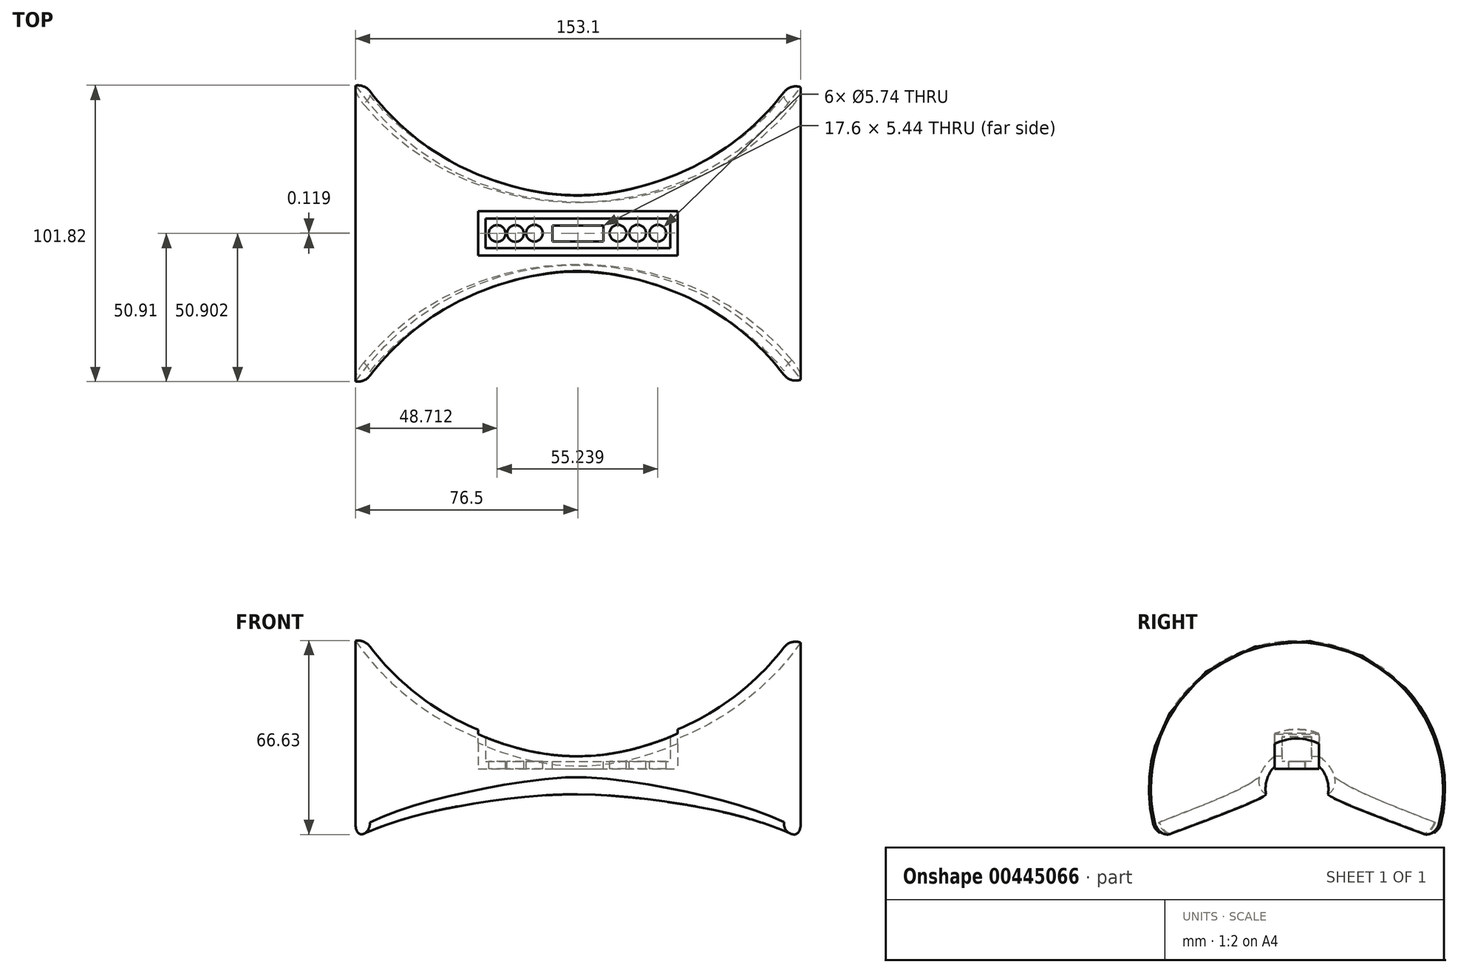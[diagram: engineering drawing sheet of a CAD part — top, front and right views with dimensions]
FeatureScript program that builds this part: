
annotation { "Feature Type Name" : "Feature", "Feature Type Description" : "" }
export const myFeature = defineFeature(function(context is Context, id is Id, definition is map)
    precondition{}
    {
        {
            var Q0;
            Q0=qCreatedBy(makeId("Top.planeOp"),FACE);
            var sketch = newSketch(context, id + "F0", { "sketchPlane" : qUnion([Q0])});
            skArc(sketch, "E0", {"start": v(-76.4, 55.95) * mm, "mid": v(-0.07, 13.52) * mm, "end": v(76.1, 56.25) * mm});
            skArc(sketch, "E1", {"start": v(-76.5, 50.83) * mm, "mid": v(-0.1, 10.81) * mm, "end": v(76.6, 50.23) * mm});
            skLineSegment(sketch, "E2", {"start": v(-76.5, 50.83) * mm, "end": v(-76.4, 55.95) * mm});
            skLineSegment(sketch, "E3", {"start": v(76.6, 50.23) * mm, "end": v(76.1, 56.25) * mm});
            skSolve(sketch);
        }
        {
            var Q0;
            Q0=qCreatedBy(makeId("Top.planeOp"),FACE);
            var sketch = newSketch(context, id + "F1", { "sketchPlane" : qUnion([Q0])});
            skLineSegment(sketch, "E4", {"start": v(-75, 0) * mm, "end": v(73.3, 0) * mm});
            skSolve(sketch);
        }
        {
            var Q0;
            Q0=makeQuery(id+"F0.imprint","IMPRINT",FACE,{"disambiguationData":[TD([[makeQuery(id+"F0.imprint","IMPRINT",EDGE,{"derivedFrom":sQuery(id+"F0.wireOp",EDGE,"E0")}),-1.0]])]});
            var Q1;
            Q1=sQuery(id+"F1.wireOp",EDGE,"E4");
            revolve(context, id + "F2", {"entities" : qUnion([Q0]), "axis" : qUnion([Q1]), "revolveType" : RevolveType.TWO_DIRECTIONS, "angle" : 200 * degree, "angleBack" : 340 * degree});
        }
        {
            var Q0;
            Q0=qCreatedBy(makeId("Top.planeOp"),FACE);
            cPlane(context, id + "F3", {"entities" : qUnion([Q0]), "cplaneType" : CPlaneType.OFFSET, "offset" : 6.86 * mm, "width" : 152.4 * mm, "height" : 152.4 * mm});
        }
        {
            var Q0;
            Q0=qCreatedBy(id+"F3.planeOp",FACE);
            var sketch = newSketch(context, id + "F4", { "sketchPlane" : qUnion([Q0])});
            skLineSegment(sketch, "E5.bottom", {"start": v(-34.3, 7.62) * mm, "end": v(34.3, 7.62) * mm});
            skLineSegment(sketch, "E5.top", {"start": v(-34.3, -7.62) * mm, "end": v(34.3, -7.62) * mm});
            skLineSegment(sketch, "E5.left", {"start": v(-34.3, 7.62) * mm, "end": v(-34.3, -7.62) * mm});
            skLineSegment(sketch, "E5.right", {"start": v(34.3, 7.62) * mm, "end": v(34.3, -7.62) * mm});
            skPoint(sketch, "E5.middle", {"position": v(0, 0) * mm});
            skSolve(sketch);
        }
        {
            var Q0;
            Q0 = qSketchRegion(id + "F4", true);
            extrude(context, id + "F5", {"entities" : qUnion([Q0]), "operationType" : NewBodyOperationType.ADD, "depth" : 25.4 * mm});
        }
        {
            var Q0;
            Q0=makeQuery(id+"F5.opExtrude","CAP_FACE",FACE,{"disambiguationData":[OSD([sQuery(id+"F4.wireOp",EDGE,"E5.bottom"),sQuery(id+"F4.wireOp",EDGE,"E5.top"),sQuery(id+"F4.wireOp",EDGE,"E5.left"),sQuery(id+"F4.wireOp",EDGE,"E5.right")])],"isStart":false});
            shell(context, id + "F6", {"entities" : qUnion([Q0]), "thickness" : 2.54 * mm});
        }
        {
            var Q0;
            {var subQ2=sQuery(id+"F4.wireOp",EDGE,"E5.top");Q0=makeQuery(id+"F5.boolean.opBoolean","SPLIT",FACE,{"disambiguationData":[TD([makeQuery(id+"F2.opRevolve","SWEPT_FACE",FACE,{"disambiguationData":[OSD([sQuery(id+"F0.wireOp",EDGE,"E0")])]})])],"derivedFrom":makeQuery(id+"F5.opExtrude","SWEPT_FACE",FACE,{"disambiguationData":[OSD([subQ2])]})});}
            extrude(context, id + "F7", {"entities" : qUnion([Q0]), "operationType" : NewBodyOperationType.REMOVE, "oppositeDirection" : true, "depth" : 25.4 * mm});
        }
        {
            var Q0;
            Q0=makeQuery(id+"F6.opShell","OFFSET_FACE",FACE,{"disambiguationData":[OSD([sQuery(id+"F4.wireOp",EDGE,"E5.bottom"),sQuery(id+"F4.wireOp",EDGE,"E5.top"),sQuery(id+"F4.wireOp",EDGE,"E5.left"),sQuery(id+"F4.wireOp",EDGE,"E5.right")])]});
            var sketch = newSketch(context, id + "F8", { "sketchPlane" : qUnion([Q0])});
            skCircle(sketch, "E6", {"center": v(-27.79, 0) * mm, "radius": 2.87 * mm});
            skPoint(sketch, "E6.centerSnap0", {"position": v(-31.75, 0) * mm});
            skCircle(sketch, "E7", {"center": v(-21.5, 0) * mm, "radius": 2.87 * mm});
            skCircle(sketch, "E8", {"center": v(-14.97, 0.11) * mm, "radius": 2.87 * mm});
            skCircle(sketch, "E9", {"center": v(27.45, 0.11) * mm, "radius": 2.87 * mm});
            skCircle(sketch, "E10", {"center": v(20.51, 0.11) * mm, "radius": 2.87 * mm});
            skCircle(sketch, "E11", {"center": v(13.75, 0.11) * mm, "radius": 2.87 * mm});
            skLineSegment(sketch, "E12.bottom", {"start": v(-8.8, 2.72) * mm, "end": v(8.8, 2.72) * mm});
            skLineSegment(sketch, "E12.top", {"start": v(-8.8, -2.72) * mm, "end": v(8.8, -2.72) * mm});
            skLineSegment(sketch, "E12.left", {"start": v(-8.8, 2.72) * mm, "end": v(-8.8, -2.72) * mm});
            skLineSegment(sketch, "E12.right", {"start": v(8.8, 2.72) * mm, "end": v(8.8, -2.72) * mm});
            skPoint(sketch, "E12.middle", {"position": v(0, 0) * mm});
            skSolve(sketch);
        }
        {
            var Q0;
            Q0=makeQuery(id+"F8.imprint","IMPRINT",FACE,{"disambiguationData":[TD([[makeQuery(id+"F8.imprint","IMPRINT",EDGE,{"derivedFrom":sQuery(id+"F8.wireOp",EDGE,"E6")}),1.0]])]});
            var Q1;
            Q1=makeQuery(id+"F8.imprint","IMPRINT",FACE,{"disambiguationData":[TD([[makeQuery(id+"F8.imprint","IMPRINT",EDGE,{"derivedFrom":sQuery(id+"F8.wireOp",EDGE,"E7")}),1.0]])]});
            var Q2;
            Q2=makeQuery(id+"F8.imprint","IMPRINT",FACE,{"disambiguationData":[TD([[makeQuery(id+"F8.imprint","IMPRINT",EDGE,{"derivedFrom":sQuery(id+"F8.wireOp",EDGE,"E8")}),1.0]])]});
            var Q3;
            Q3=makeQuery(id+"F8.imprint","IMPRINT",FACE,{"disambiguationData":[TD([[makeQuery(id+"F8.imprint","IMPRINT",EDGE,{"derivedFrom":sQuery(id+"F8.wireOp",EDGE,"E12.bottom")}),-1.0]])]});
            var Q4;
            Q4=makeQuery(id+"F8.imprint","IMPRINT",FACE,{"disambiguationData":[TD([[makeQuery(id+"F8.imprint","IMPRINT",EDGE,{"derivedFrom":sQuery(id+"F8.wireOp",EDGE,"E11")}),1.0]])]});
            var Q5;
            Q5=makeQuery(id+"F8.imprint","IMPRINT",FACE,{"disambiguationData":[TD([[makeQuery(id+"F8.imprint","IMPRINT",EDGE,{"derivedFrom":sQuery(id+"F8.wireOp",EDGE,"E10")}),1.0]])]});
            var Q6;
            Q6=makeQuery(id+"F8.imprint","IMPRINT",FACE,{"disambiguationData":[TD([[makeQuery(id+"F8.imprint","IMPRINT",EDGE,{"derivedFrom":sQuery(id+"F8.wireOp",EDGE,"E9")}),1.0]])]});
            extrude(context, id + "F9", {"entities" : qUnion([Q0, Q1, Q2, Q3, Q4, Q5, Q6]), "operationType" : NewBodyOperationType.REMOVE, "oppositeDirection" : true, "depth" : 25.4 * mm});
        }
        {
            var Q0;
            Q0=makeQuery(id+"F2.opRevolve","SWEPT_EDGE",EDGE,{"disambiguationData":[OSD([sQuery(id+"F0.wireOp",EDGE,"E0"),sQuery(id+"F0.wireOp",EDGE,"E2")])]});
            var Q1;
            Q1=makeQuery(id+"F2.opRevolve","SWEPT_EDGE",EDGE,{"disambiguationData":[OSD([sQuery(id+"F0.wireOp",EDGE,"E0"),sQuery(id+"F0.wireOp",EDGE,"E3")])]});
            fillet(context, id + "F10", {"entities" : qUnion([Q0, Q1]), "radius" : 5.08 * mm, "tangentPropagation" : true, "allowEdgeOverflow" : false});
        }
        {
            var Q0;
            Q0=makeQuery(id+"F2.opRevolve","CAP_EDGE",EDGE,{"disambiguationData":[OSD([sQuery(id+"F0.wireOp",EDGE,"E0")])],"isStart":true});
            var Q1;
            Q1=makeQuery(id+"F2.opRevolve","CAP_EDGE",EDGE,{"disambiguationData":[OSD([sQuery(id+"F0.wireOp",EDGE,"E0")])],"isStart":false});
            fillet(context, id + "F11", {"entities" : qUnion([Q0, Q1]), "radius" : 5.08 * mm, "tangentPropagation" : true, "allowEdgeOverflow" : false});
        }
    });
